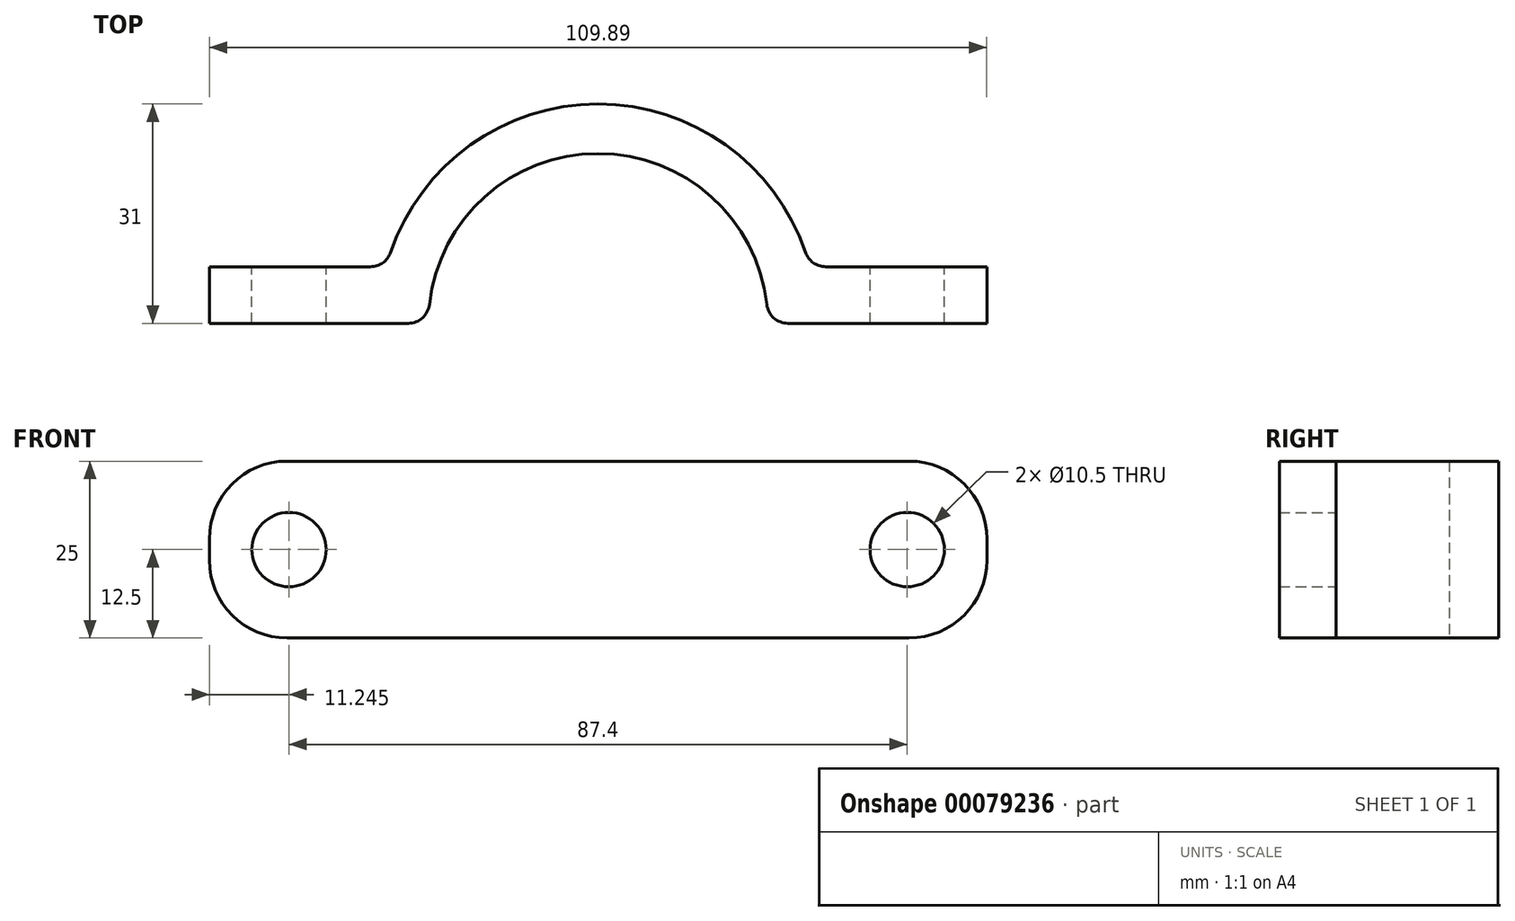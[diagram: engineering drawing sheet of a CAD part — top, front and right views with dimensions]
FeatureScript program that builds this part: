
annotation { "Feature Type Name" : "Feature", "Feature Type Description" : "" }
export const myFeature = defineFeature(function(context is Context, id is Id, definition is map)
    precondition{}
    {
        {
            var Q0;
            Q0=qCreatedBy(makeId("Top.planeOp"),FACE);
            var sketch = newSketch(context, id + "F0", { "sketchPlane" : qUnion([Q0])});
            skLineSegment(sketch, "E0.bottom", {"start": v(-11.48, 44.08) * mm, "end": v(-11.48, 44.08) * mm});
            skLineSegment(sketch, "E0.left", {"start": v(-42.48, 13.08) * mm, "end": v(-42.48, 13.08) * mm});
            skLineSegment(sketch, "E0.right", {"start": v(19.52, 13.08) * mm, "end": v(19.52, 13.08) * mm});
            skPoint(sketch, "E1.visualSharp", {"position": v(-42.48, 44.08) * mm});
            skArc(sketch, "E1.filletArc", {"start": v(-11.48, 44.08) * mm, "mid": v(-33.4, 35) * mm, "end": v(-42.48, 13.08) * mm});
            skPoint(sketch, "E2.visualSharp", {"position": v(19.52, 44.08) * mm});
            skArc(sketch, "E2.filletArc", {"start": v(19.52, 13.08) * mm, "mid": v(10.45, 35) * mm, "end": v(-11.48, 44.08) * mm});
            skPoint(sketch, "E3", {"position": v(-41.42, 21.08) * mm});
            skPoint(sketch, "E4", {"position": v(18.47, 21.08) * mm});
            skLineSegment(sketch, "E5", {"start": v(-41.42, 21.08) * mm, "end": v(-66.42, 21.08) * mm});
            skLineSegment(sketch, "E6", {"start": v(-66.42, 21.08) * mm, "end": v(-66.42, 13.08) * mm});
            skLineSegment(sketch, "E7", {"start": v(-66.42, 13.08) * mm, "end": v(-42.48, 13.08) * mm});
            skLineSegment(sketch, "E8", {"start": v(19.52, 13.08) * mm, "end": v(43.47, 13.08) * mm});
            skLineSegment(sketch, "E9", {"start": v(43.47, 13.08) * mm, "end": v(43.47, 21.08) * mm});
            skLineSegment(sketch, "E10", {"start": v(43.47, 21.08) * mm, "end": v(18.47, 21.08) * mm});
            skLineSegment(sketch, "E11.bottom", {"start": v(-11.48, 37.08) * mm, "end": v(-11.48, 37.08) * mm});
            skLineSegment(sketch, "E11.left", {"start": v(-35.48, 13.08) * mm, "end": v(-35.48, 13.08) * mm});
            skLineSegment(sketch, "E11.right", {"start": v(12.52, 13.08) * mm, "end": v(12.52, 13.08) * mm});
            skPoint(sketch, "E12.visualSharp", {"position": v(12.52, 37.08) * mm});
            skArc(sketch, "E12.filletArc", {"start": v(12.52, 13.08) * mm, "mid": v(5.5, 30.05) * mm, "end": v(-11.48, 37.08) * mm});
            skPoint(sketch, "E13.visualSharp", {"position": v(-35.48, 37.08) * mm});
            skArc(sketch, "E13.filletArc", {"start": v(-11.48, 37.08) * mm, "mid": v(-28.45, 30.05) * mm, "end": v(-35.48, 13.08) * mm});
            skLineSegment(sketch, "E14", {"start": v(-35.48, 13.08) * mm, "end": v(-42.48, 13.08) * mm});
            skLineSegment(sketch, "E15", {"start": v(12.52, 13.08) * mm, "end": v(19.52, 13.08) * mm});
            skSolve(sketch);
        }
        {
            var Q0;
            {var subQ2=sQuery(id+"F0.wireOp",EDGE,"E5");Q0=makeQuery(id+"F0.imprint","IMPRINT",FACE,{"disambiguationData":[TD([[makeQuery(id+"F0.imprint","IMPRINT",EDGE,{"derivedFrom":subQ2}),1.0]])]});}
            var Q1;
            {var subQ0=sQuery(id+"F0.wireOp",EDGE,"E8");Q1=makeQuery(id+"F0.imprint","IMPRINT",FACE,{"disambiguationData":[TD([[makeQuery(id+"F0.imprint","IMPRINT",EDGE,{"derivedFrom":subQ0}),1.0]])]});}
            var Q2;
            Q2=makeQuery(id+"F0.imprint","IMPRINT",FACE,{"disambiguationData":[TD([[makeQuery(id+"F0.imprint","IMPRINT",EDGE,{"derivedFrom":sQuery(id+"F0.wireOp",EDGE,"E12.filletArc")}),-1.0]])]});
            extrude(context, id + "F1", {"entities" : qUnion([Q0, Q1, Q2]), "depth" : 25 * mm});
        }
        {
            var Q0;
            Q0=makeQuery(id+"F1.opExtrude","CAP_EDGE",EDGE,{"disambiguationData":[OSD([sQuery(id+"F0.wireOp",EDGE,"E9")])],"isStart":true});
            var Q1;
            Q1=makeQuery(id+"F1.opExtrude","CAP_EDGE",EDGE,{"disambiguationData":[OSD([sQuery(id+"F0.wireOp",EDGE,"E9")])],"isStart":false});
            var Q2;
            Q2=makeQuery(id+"F1.opExtrude","CAP_EDGE",EDGE,{"disambiguationData":[OSD([sQuery(id+"F0.wireOp",EDGE,"E6")])],"isStart":false});
            var Q3;
            Q3=makeQuery(id+"F1.opExtrude","CAP_EDGE",EDGE,{"disambiguationData":[OSD([sQuery(id+"F0.wireOp",EDGE,"E6")])],"isStart":true});
            fillet(context, id + "F2", {"entities" : qUnion([Q0, Q1, Q2, Q3]), "radius" : 11 * mm, "tangentPropagation" : true, "allowEdgeOverflow" : false});
        }
        {
            var Q0;
            Q0=makeQuery(id+"F1.opExtrude","SWEPT_EDGE",EDGE,{"disambiguationData":[OSD([sQuery(id+"F0.wireOp",EDGE,"E13.filletArc"),sQuery(id+"F0.wireOp",EDGE,"E14")])]});
            var Q1;
            Q1=makeQuery(id+"F1.opExtrude","SWEPT_EDGE",EDGE,{"disambiguationData":[OSD([sQuery(id+"F0.wireOp",EDGE,"E12.filletArc"),sQuery(id+"F0.wireOp",EDGE,"E15")])]});
            fillet(context, id + "F3", {"entities" : qUnion([Q0, Q1]), "radius" : 3 * mm, "tangentPropagation" : true, "allowEdgeOverflow" : false});
        }
        {
            var Q0;
            Q0=makeQuery(id+"F1.opExtrude","SWEPT_EDGE",EDGE,{"disambiguationData":[OSD([sQuery(id+"F0.wireOp",EDGE,"E1.filletArc"),sQuery(id+"F0.wireOp",EDGE,"E5")])]});
            var Q1;
            Q1=makeQuery(id+"F1.opExtrude","SWEPT_EDGE",EDGE,{"disambiguationData":[OSD([sQuery(id+"F0.wireOp",EDGE,"E2.filletArc"),sQuery(id+"F0.wireOp",EDGE,"E10")])]});
            fillet(context, id + "F4", {"entities" : qUnion([Q0, Q1]), "radius" : 3 * mm, "tangentPropagation" : true, "allowEdgeOverflow" : false});
        }
        {
            var Q0;
            Q0=makeQuery(id+"F1.opExtrude","SWEPT_FACE",FACE,{"disambiguationData":[OSD([sQuery(id+"F0.wireOp",EDGE,"E5")])]});
            var sketch = newSketch(context, id + "F5", { "sketchPlane" : qUnion([Q0])});
            skPoint(sketch, "E16", {"position": v(55.17, 12.5) * mm});
            skPoint(sketch, "E17", {"position": v(-32.22, 12.5) * mm});
            skSolve(sketch);
        }
        {
            var Q0;
            Q0=sQuery(id+"F5.wireOp",VERTEX,"E16");
            var Q1;
            Q1=sQuery(id+"F5.wireOp",VERTEX,"E17");
            var Q2;
            Q2=makeQuery(id+"F1.opExtrude","SWEPT_BODY",BODY,{"disambiguationData":[OSD([sQuery(id+"F0.wireOp",EDGE,"E1.filletArc"),sQuery(id+"F0.wireOp",EDGE,"E2.filletArc"),sQuery(id+"F0.wireOp",EDGE,"E5"),sQuery(id+"F0.wireOp",EDGE,"E6"),sQuery(id+"F0.wireOp",EDGE,"E7"),sQuery(id+"F0.wireOp",EDGE,"E8"),sQuery(id+"F0.wireOp",EDGE,"E9"),sQuery(id+"F0.wireOp",EDGE,"E10"),sQuery(id+"F0.wireOp",EDGE,"E12.filletArc"),sQuery(id+"F0.wireOp",EDGE,"E13.filletArc"),sQuery(id+"F0.wireOp",EDGE,"E14"),sQuery(id+"F0.wireOp",EDGE,"E15")])]});
            hole(context, id + "F6", {"style" : HoleStyle.SIMPLE, "endStyle" : HoleEndStyle.THROUGH, "holeDiameter" : 10.5 * mm, "locations" : qUnion([Q0, Q1]), "scope" : qUnion([Q2]), "isTappedThrough" : true});
        }
    });
